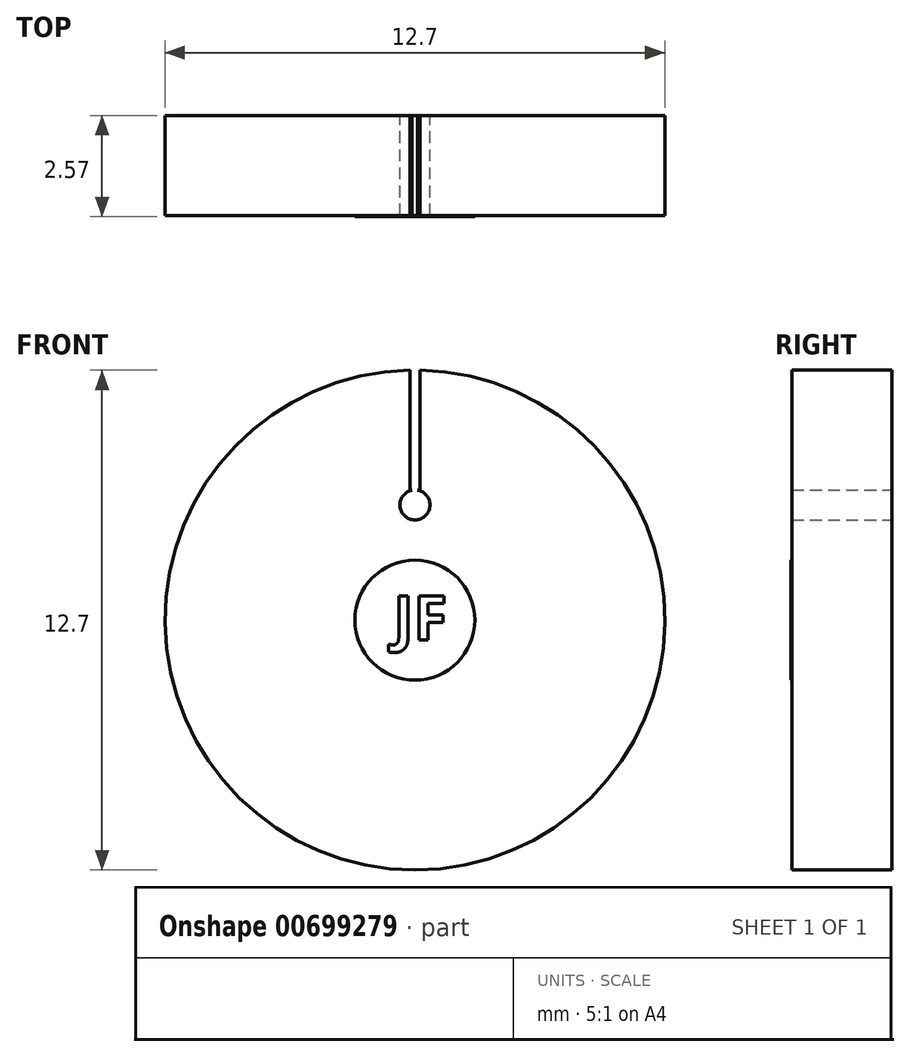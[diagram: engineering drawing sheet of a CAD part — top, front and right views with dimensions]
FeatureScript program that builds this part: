
annotation { "Feature Type Name" : "Feature", "Feature Type Description" : "" }
export const myFeature = defineFeature(function(context is Context, id is Id, definition is map)
    precondition{}
    {
        {
            var Q0;
            Q0=qCreatedBy(makeId("Front.planeOp"),FACE);
            var sketch = newSketch(context, id + "F0", { "sketchPlane" : qUnion([Q0])});
            skCircle(sketch, "E0", {"center": v(0, 0) * mm, "radius": 6.35 * mm});
            skSolve(sketch);
        }
        {
            var Q0;
            Q0 = qSketchRegion(id + "F0", true);
            extrude(context, id + "F1", {"entities" : qUnion([Q0]), "depth" : 2.54 * mm, "offsetDistance" : 25.4 * mm});
        }
        {
            var Q0;
            Q0=qCreatedBy(makeId("Front.planeOp"),FACE);
            var sketch = newSketch(context, id + "F2", { "sketchPlane" : qUnion([Q0])});
            skCircle(sketch, "E1", {"center": v(0, 2.93) * mm, "radius": 0.38 * mm});
            skSolve(sketch);
        }
        {
            var Q0;
            Q0 = qSketchRegion(id + "F2", true);
            extrude(context, id + "F3", {"entities" : qUnion([Q0]), "operationType" : NewBodyOperationType.REMOVE, "depth" : 11.94 * mm, "offsetDistance" : 25.4 * mm});
        }
        {
            var Q0;
            Q0=qCreatedBy(makeId("Front.planeOp"),FACE);
            var sketch = newSketch(context, id + "F4", { "sketchPlane" : qUnion([Q0])});
            skLineSegment(sketch, "E2", {"start": v(-0.13, 3.3) * mm, "end": v(-0.13, 6.56) * mm});
            skLineSegment(sketch, "E3", {"start": v(-0.13, 6.56) * mm, "end": v(0.13, 6.56) * mm});
            skLineSegment(sketch, "E4", {"start": v(0.13, 6.56) * mm, "end": v(0.13, 3.3) * mm});
            skLineSegment(sketch, "E5", {"start": v(0.13, 3.3) * mm, "end": v(-0.13, 3.3) * mm});
            skSolve(sketch);
        }
        {
            var Q0;
            Q0 = qSketchRegion(id + "F4", true);
            extrude(context, id + "F5", {"entities" : qUnion([Q0]), "operationType" : NewBodyOperationType.REMOVE, "depth" : 10.77 * mm, "offsetDistance" : 25.4 * mm});
        }
        {
            var Q0;
            Q0=qCreatedBy(makeId("Front.planeOp"),FACE);
            var sketch = newSketch(context, id + "F6", { "sketchPlane" : qUnion([Q0])});
            skCircle(sketch, "E6", {"center": v(0, 0) * mm, "radius": 1.52 * mm});
            skText(sketch, "E7", { "text": "JF", "fontName": "OpenSans-Bold.ttf"});
            const initialGuessF6  = {"E7": [-0.00055, -0.0005, 1, 0, 0.00112]};
            skSetInitialGuess(sketch, initialGuessF6);
            skSolve(sketch);
        }
        {
            var Q0;
            Q0 = qSketchRegion(id + "F6", true);
            extrude(context, id + "F7", {"entities" : qUnion([Q0]), "operationType" : NewBodyOperationType.ADD, "depth" : 2.57 * mm, "offsetDistance" : 25.4 * mm});
        }
    });
